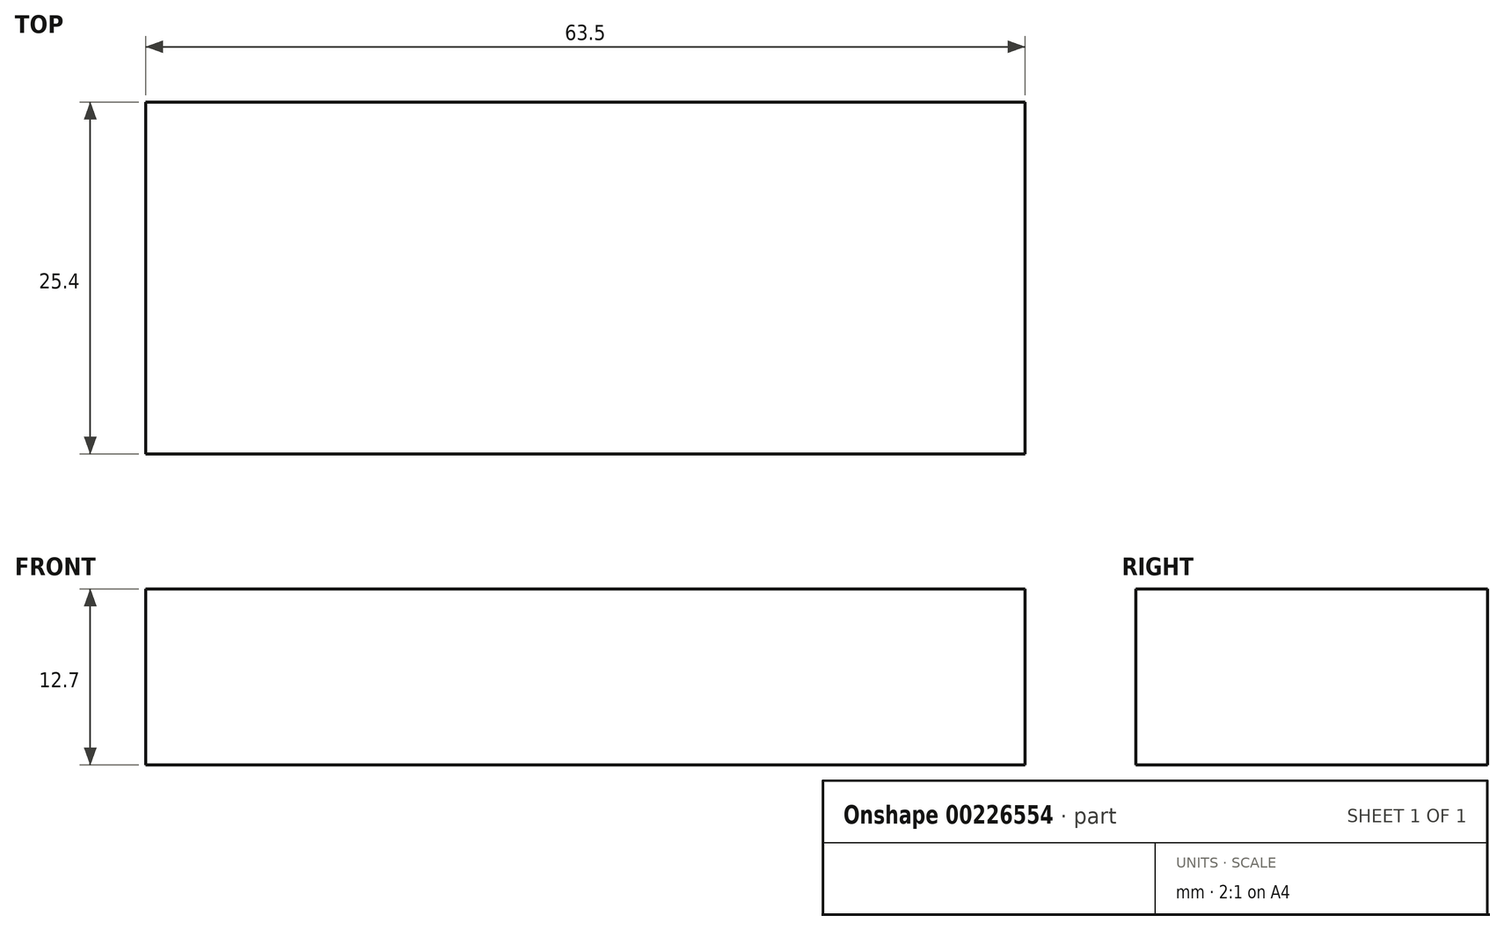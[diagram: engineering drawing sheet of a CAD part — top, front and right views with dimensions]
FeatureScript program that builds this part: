
annotation { "Feature Type Name" : "Feature", "Feature Type Description" : "" }
export const myFeature = defineFeature(function(context is Context, id is Id, definition is map)
    precondition{}
    {
        {
            var Q0;
            Q0=qCreatedBy(makeId("Front.planeOp"),FACE);
            var sketch = newSketch(context, id + "F0", { "sketchPlane" : qUnion([Q0])});
            skLineSegment(sketch, "E0.bottom", {"start": v(0, 0) * mm, "end": v(63.5, 0) * mm});
            skLineSegment(sketch, "E0.top", {"start": v(0, 12.7) * mm, "end": v(63.5, 12.7) * mm});
            skLineSegment(sketch, "E0.left", {"start": v(0, 0) * mm, "end": v(0, 12.7) * mm});
            skLineSegment(sketch, "E0.right", {"start": v(63.5, 0) * mm, "end": v(63.5, 12.7) * mm});
            skSolve(sketch);
        }
        {
            var Q0;
            Q0=makeQuery(id+"F0.imprint","IMPRINT",FACE,{"disambiguationData":[TD([[makeQuery(id+"F0.imprint","IMPRINT",EDGE,{"derivedFrom":sQuery(id+"F0.wireOp",EDGE,"E0.bottom")}),1.0]])]});
            extrude(context, id + "F1", {"entities" : qUnion([Q0]), "oppositeDirection" : true, "depth" : 25.4 * mm});
        }
    });
